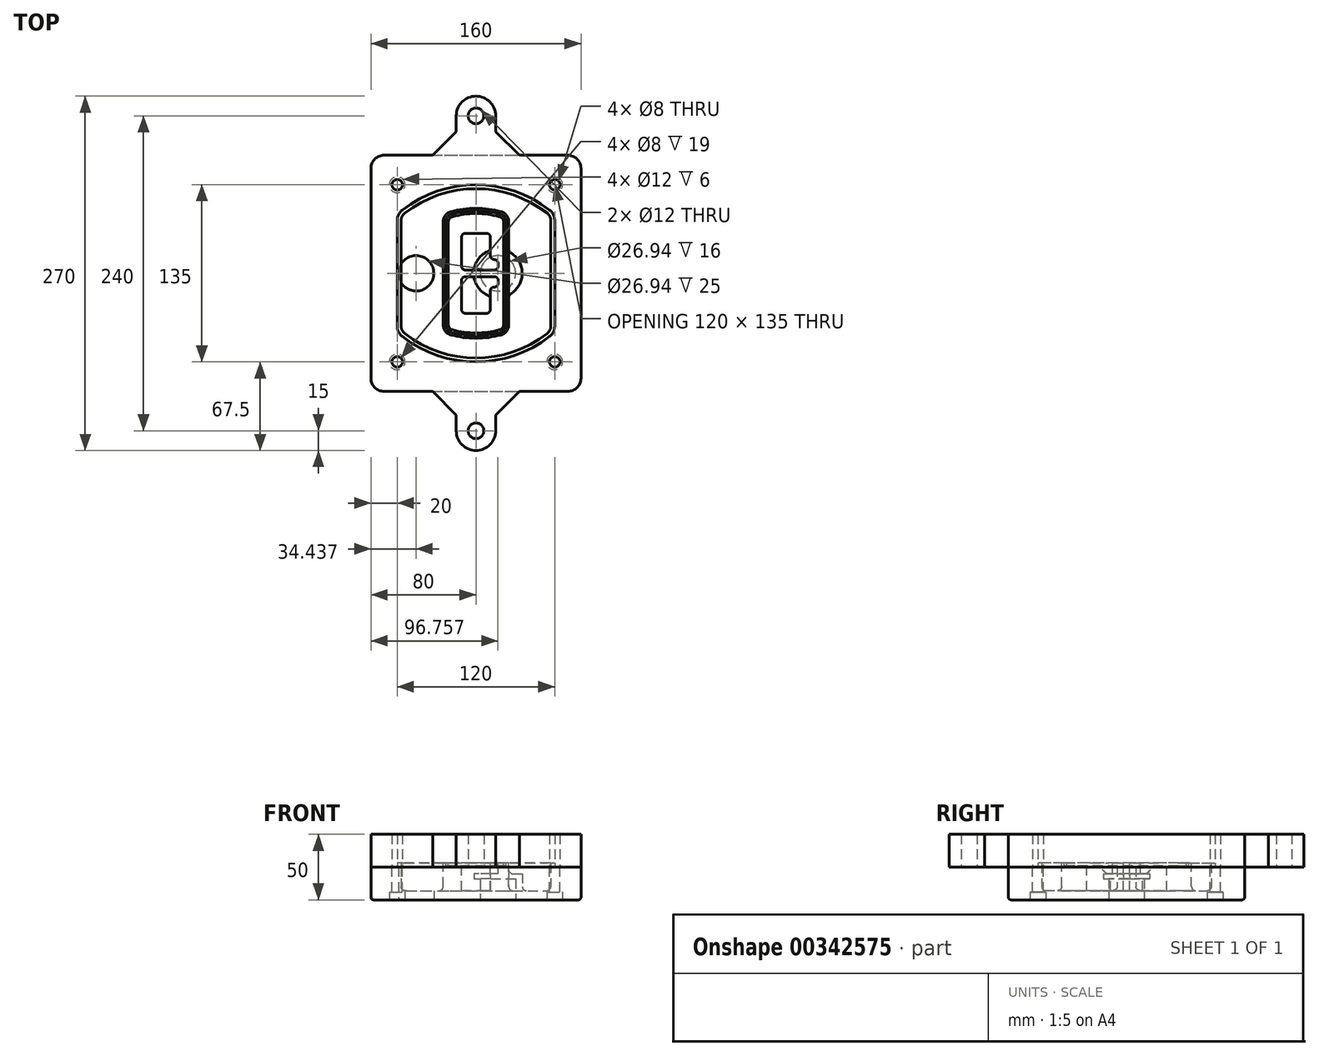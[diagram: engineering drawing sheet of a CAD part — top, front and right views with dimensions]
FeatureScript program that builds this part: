
annotation { "Feature Type Name" : "Feature", "Feature Type Description" : "" }
export const myFeature = defineFeature(function(context is Context, id is Id, definition is map)
    precondition{}
    {
        {
            var Q0;
            Q0=qCreatedBy(makeId("Top.planeOp"),FACE);
            var sketch = newSketch(context, id + "F0", { "sketchPlane" : qUnion([Q0])});
            skPoint(sketch, "E0.rect.middle", {"position": v(0, 0) * mm});
            skLineSegment(sketch, "E1.bottom", {"start": v(-70, -90) * mm, "end": v(70, -90) * mm});
            skLineSegment(sketch, "E1.top", {"start": v(-70, 90) * mm, "end": v(70, 90) * mm});
            skLineSegment(sketch, "E1.left", {"start": v(-80, -80) * mm, "end": v(-80, 80) * mm});
            skLineSegment(sketch, "E1.right", {"start": v(80, -80) * mm, "end": v(80, 80) * mm});
            skLineSegment(sketch, "E2", {"start": v(-80, 90) * mm, "end": v(80, -90) * mm, "construction": true});
            skLineSegment(sketch, "E3", {"start": v(80, 90) * mm, "end": v(-80, -90) * mm, "construction": true});
            skCircle(sketch, "E4", {"center": v(-60, 67.5) * mm, "radius": 4 * mm});
            skCircle(sketch, "E5", {"center": v(60, 67.5) * mm, "radius": 4 * mm});
            skCircle(sketch, "E6", {"center": v(60, -67.5) * mm, "radius": 4 * mm});
            skCircle(sketch, "E7", {"center": v(-60, -67.5) * mm, "radius": 4 * mm});
            skLineSegment(sketch, "E8", {"start": v(-60, 67.5) * mm, "end": v(60, 67.5) * mm, "construction": true});
            skLineSegment(sketch, "E9", {"start": v(60, 67.5) * mm, "end": v(60, -67.5) * mm, "construction": true});
            skLineSegment(sketch, "E10", {"start": v(60, -67.5) * mm, "end": v(-60, -67.5) * mm, "construction": true});
            skLineSegment(sketch, "E11", {"start": v(-60, -67.5) * mm, "end": v(-60, 67.5) * mm, "construction": true});
            skLineSegment(sketch, "E12", {"start": v(-60, 40.3) * mm, "end": v(-60, -40.3) * mm});
            skLineSegment(sketch, "E13", {"start": v(60, 40.3) * mm, "end": v(60, -40.3) * mm});
            skArc(sketch, "E14", {"start": v(56.15, 48.18) * mm, "mid": v(0, 67.5) * mm, "end": v(-56.15, 48.18) * mm});
            skArc(sketch, "E15", {"start": v(-56.15, -48.18) * mm, "mid": v(0, -67.5) * mm, "end": v(56.15, -48.18) * mm});
            skLineSegment(sketch, "E16", {"start": v(-60, 0) * mm, "end": v(60, 0) * mm, "construction": true});
            skPoint(sketch, "E17.visualSharp", {"position": v(-60, -45) * mm});
            skArc(sketch, "E17.filletArc", {"start": v(-60, -40.3) * mm, "mid": v(-58.99, -44.68) * mm, "end": v(-56.15, -48.18) * mm});
            skPoint(sketch, "E18.visualSharp", {"position": v(-60, 45) * mm});
            skArc(sketch, "E18.filletArc", {"start": v(-56.15, 48.18) * mm, "mid": v(-58.99, 44.68) * mm, "end": v(-60, 40.3) * mm});
            skPoint(sketch, "E19.visualSharp", {"position": v(60, 45) * mm});
            skArc(sketch, "E19.filletArc", {"start": v(60, 40.3) * mm, "mid": v(58.99, 44.68) * mm, "end": v(56.15, 48.18) * mm});
            skPoint(sketch, "E20.visualSharp", {"position": v(60, -45) * mm});
            skArc(sketch, "E20.filletArc", {"start": v(56.15, -48.18) * mm, "mid": v(58.99, -44.68) * mm, "end": v(60, -40.3) * mm});
            skPoint(sketch, "E21.visualSharp", {"position": v(-80, 90) * mm});
            skArc(sketch, "E21.filletArc", {"start": v(-70, 90) * mm, "mid": v(-77.07, 87.07) * mm, "end": v(-80, 80) * mm});
            skPoint(sketch, "E22.visualSharp", {"position": v(80, 90) * mm});
            skArc(sketch, "E22.filletArc", {"start": v(80, 80) * mm, "mid": v(77.07, 87.07) * mm, "end": v(70, 90) * mm});
            skPoint(sketch, "E23.visualSharp", {"position": v(80, -90) * mm});
            skArc(sketch, "E23.filletArc", {"start": v(70, -90) * mm, "mid": v(77.07, -87.07) * mm, "end": v(80, -80) * mm});
            skPoint(sketch, "E24.visualSharp", {"position": v(-80, -90) * mm});
            skArc(sketch, "E24.filletArc", {"start": v(-80, -80) * mm, "mid": v(-77.07, -87.07) * mm, "end": v(-70, -90) * mm});
            skArc(sketch, "E25.0", {"start": v(57, 40.3) * mm, "mid": v(56.3, 43.36) * mm, "end": v(54.3, 45.81) * mm});
            skLineSegment(sketch, "E25.1", {"start": v(57, 40.3) * mm, "end": v(57, -40.3) * mm});
            skArc(sketch, "E25.2", {"start": v(54.3, -45.81) * mm, "mid": v(56.3, -43.36) * mm, "end": v(57, -40.3) * mm});
            skArc(sketch, "E25.3", {"start": v(-54.3, -45.81) * mm, "mid": v(0, -64.5) * mm, "end": v(54.3, -45.81) * mm});
            skArc(sketch, "E25.4", {"start": v(-57, -40.3) * mm, "mid": v(-56.3, -43.36) * mm, "end": v(-54.3, -45.81) * mm});
            skArc(sketch, "E25.5", {"start": v(54.3, 45.81) * mm, "mid": v(0, 64.5) * mm, "end": v(-54.3, 45.81) * mm});
            skLineSegment(sketch, "E25.6", {"start": v(-57, 40.3) * mm, "end": v(-57, -40.3) * mm});
            skArc(sketch, "E25.7", {"start": v(-54.3, 45.81) * mm, "mid": v(-56.3, 43.36) * mm, "end": v(-57, 40.3) * mm});
            skArc(sketch, "E26.0", {"start": v(-58.62, 51.33) * mm, "mid": v(-62.58, 46.43) * mm, "end": v(-64, 40.3) * mm});
            skArc(sketch, "E26.1", {"start": v(58.62, 51.33) * mm, "mid": v(0, 71.5) * mm, "end": v(-58.62, 51.33) * mm});
            skArc(sketch, "E26.2", {"start": v(64, 40.3) * mm, "mid": v(62.58, 46.43) * mm, "end": v(58.62, 51.33) * mm});
            skLineSegment(sketch, "E26.3", {"start": v(64, 40.3) * mm, "end": v(64, -40.3) * mm});
            skArc(sketch, "E26.4", {"start": v(58.62, -51.33) * mm, "mid": v(62.58, -46.43) * mm, "end": v(64, -40.3) * mm});
            skLineSegment(sketch, "E26.5", {"start": v(-64, 40.3) * mm, "end": v(-64, -40.3) * mm});
            skArc(sketch, "E26.6", {"start": v(-58.62, -51.33) * mm, "mid": v(0, -71.5) * mm, "end": v(58.62, -51.33) * mm});
            skArc(sketch, "E26.7", {"start": v(-64, -40.3) * mm, "mid": v(-62.58, -46.43) * mm, "end": v(-58.62, -51.33) * mm});
            skSolve(sketch);
        }
        {
            var Q0;
            Q0=makeQuery(id+"F0.imprint","IMPRINT",FACE,{"disambiguationData":[TD([[makeQuery(id+"F0.imprint","IMPRINT",EDGE,{"derivedFrom":sQuery(id+"F0.wireOp",EDGE,"E1.bottom")}),1.0]])]});
            var Q1;
            Q1=makeQuery(id+"F0.imprint","IMPRINT",FACE,{"disambiguationData":[TD([[makeQuery(id+"F0.imprint","IMPRINT",EDGE,{"derivedFrom":sQuery(id+"F0.wireOp",EDGE,"E12")}),1.0]])]});
            var Q2;
            Q2=makeQuery(id+"F0.imprint","IMPRINT",FACE,{"disambiguationData":[TD([[makeQuery(id+"F0.imprint","IMPRINT",EDGE,{"derivedFrom":sQuery(id+"F0.wireOp",EDGE,"E25.0")}),1.0]])]});
            var Q3;
            Q3=makeQuery(id+"F0.imprint","IMPRINT",FACE,{"disambiguationData":[TD([[makeQuery(id+"F0.imprint","IMPRINT",EDGE,{"derivedFrom":sQuery(id+"F0.wireOp",EDGE,"E12")}),-1.0]])]});
            extrude(context, id + "F1", {"entities" : qUnion([Q0, Q1, Q2, Q3]), "oppositeDirection" : true, "depth" : 25 * mm});
        }
        {
            var Q0;
            Q0=makeQuery(id+"F0.imprint","IMPRINT",FACE,{"disambiguationData":[TD([[makeQuery(id+"F0.imprint","IMPRINT",EDGE,{"derivedFrom":sQuery(id+"F0.wireOp",EDGE,"E12")}),1.0]])]});
            extrude(context, id + "F2", {"entities" : qUnion([Q0]), "operationType" : NewBodyOperationType.ADD, "depth" : 3 * mm});
        }
        {
            var Q0;
            Q0=makeQuery(id+"F0.imprint","IMPRINT",FACE,{"disambiguationData":[TD([[makeQuery(id+"F0.imprint","IMPRINT",EDGE,{"derivedFrom":sQuery(id+"F0.wireOp",EDGE,"E25.0")}),1.0]])]});
            extrude(context, id + "F3", {"entities" : qUnion([Q0]), "operationType" : NewBodyOperationType.REMOVE, "oppositeDirection" : true, "depth" : 18 * mm});
        }
        {
            var Q0;
            Q0=makeQuery(id+"F2.opExtrude","CAP_FACE",FACE,{"disambiguationData":[OSD([sQuery(id+"F0.wireOp",EDGE,"E12"),sQuery(id+"F0.wireOp",EDGE,"E13"),sQuery(id+"F0.wireOp",EDGE,"E14"),sQuery(id+"F0.wireOp",EDGE,"E15"),sQuery(id+"F0.wireOp",EDGE,"E17.filletArc"),sQuery(id+"F0.wireOp",EDGE,"E18.filletArc"),sQuery(id+"F0.wireOp",EDGE,"E19.filletArc"),sQuery(id+"F0.wireOp",EDGE,"E20.filletArc"),sQuery(id+"F0.wireOp",EDGE,"E25.0"),sQuery(id+"F0.wireOp",EDGE,"E25.1"),sQuery(id+"F0.wireOp",EDGE,"E25.2"),sQuery(id+"F0.wireOp",EDGE,"E25.3"),sQuery(id+"F0.wireOp",EDGE,"E25.4"),sQuery(id+"F0.wireOp",EDGE,"E25.5"),sQuery(id+"F0.wireOp",EDGE,"E25.6"),sQuery(id+"F0.wireOp",EDGE,"E25.7")])],"isStart":false});
            var sketch = newSketch(context, id + "F4", { "sketchPlane" : qUnion([Q0])});
            skArc(sketch, "E27.0", {"start": v(-19.08, -46.97) * mm, "mid": v(0, -49.5) * mm, "end": v(19.08, -46.97) * mm});
            skArc(sketch, "E28.0", {"start": v(19.08, 46.97) * mm, "mid": v(0, 49.5) * mm, "end": v(-19.08, 46.97) * mm});
            skLineSegment(sketch, "E29", {"start": v(-25, 39.25) * mm, "end": v(-25, -39.25) * mm});
            skLineSegment(sketch, "E30", {"start": v(25, 39.25) * mm, "end": v(25, -39.25) * mm});
            skLineSegment(sketch, "E31", {"start": v(-25, 45.1) * mm, "end": v(25, 45.1) * mm, "construction": true});
            skLineSegment(sketch, "E32", {"start": v(-25, -45.1) * mm, "end": v(25, -45.1) * mm, "construction": true});
            skPoint(sketch, "E33.visualSharp", {"position": v(-25, 45.1) * mm});
            skArc(sketch, "E33.filletArc", {"start": v(-19.08, 46.97) * mm, "mid": v(-23.35, 44.11) * mm, "end": v(-25, 39.25) * mm});
            skPoint(sketch, "E34.visualSharp", {"position": v(25, 45.1) * mm});
            skArc(sketch, "E34.filletArc", {"start": v(25, 39.25) * mm, "mid": v(23.35, 44.11) * mm, "end": v(19.08, 46.97) * mm});
            skPoint(sketch, "E35.visualSharp", {"position": v(25, -45.1) * mm});
            skArc(sketch, "E35.filletArc", {"start": v(19.08, -46.97) * mm, "mid": v(23.35, -44.11) * mm, "end": v(25, -39.25) * mm});
            skPoint(sketch, "E36.visualSharp", {"position": v(-25, -45.1) * mm});
            skArc(sketch, "E36.filletArc", {"start": v(-25, -39.25) * mm, "mid": v(-23.35, -44.11) * mm, "end": v(-19.08, -46.97) * mm});
            skArc(sketch, "E37.0", {"start": v(54.3, 45.81) * mm, "mid": v(0, 64.5) * mm, "end": v(-54.3, 45.81) * mm});
            skArc(sketch, "E37.1", {"start": v(-54.3, 45.81) * mm, "mid": v(-56.3, 43.36) * mm, "end": v(-57, 40.3) * mm});
            skLineSegment(sketch, "E37.2", {"start": v(-57, 40.3) * mm, "end": v(-57, -40.3) * mm});
            skArc(sketch, "E37.3", {"start": v(-57, -40.3) * mm, "mid": v(-56.3, -43.36) * mm, "end": v(-54.3, -45.81) * mm});
            skArc(sketch, "E37.4", {"start": v(-54.3, -45.81) * mm, "mid": v(0, -64.5) * mm, "end": v(54.3, -45.81) * mm});
            skArc(sketch, "E37.5", {"start": v(54.3, -45.81) * mm, "mid": v(56.3, -43.36) * mm, "end": v(57, -40.3) * mm});
            skLineSegment(sketch, "E37.6", {"start": v(57, 40.3) * mm, "end": v(57, -40.3) * mm});
            skArc(sketch, "E37.7", {"start": v(57, 40.3) * mm, "mid": v(56.3, 43.36) * mm, "end": v(54.3, 45.81) * mm});
            skLineSegment(sketch, "E38.0", {"start": v(23, 39.25) * mm, "end": v(23, -39.25) * mm});
            skArc(sketch, "E38.1", {"start": v(18.56, -45.04) * mm, "mid": v(21.76, -42.9) * mm, "end": v(23, -39.25) * mm});
            skArc(sketch, "E38.2", {"start": v(-18.56, -45.04) * mm, "mid": v(0, -47.5) * mm, "end": v(18.56, -45.04) * mm});
            skArc(sketch, "E38.3", {"start": v(-23, -39.25) * mm, "mid": v(-21.76, -42.9) * mm, "end": v(-18.56, -45.04) * mm});
            skLineSegment(sketch, "E38.4", {"start": v(-23, 39.25) * mm, "end": v(-23, -39.25) * mm});
            skArc(sketch, "E38.5", {"start": v(23, 39.25) * mm, "mid": v(21.76, 42.9) * mm, "end": v(18.56, 45.04) * mm});
            skArc(sketch, "E38.6", {"start": v(-18.56, 45.04) * mm, "mid": v(-21.76, 42.9) * mm, "end": v(-23, 39.25) * mm});
            skArc(sketch, "E38.7", {"start": v(18.56, 45.04) * mm, "mid": v(0, 47.5) * mm, "end": v(-18.56, 45.04) * mm});
            skArc(sketch, "E39.0", {"start": v(21, 39.25) * mm, "mid": v(20.18, 41.68) * mm, "end": v(18.04, 43.1) * mm});
            skLineSegment(sketch, "E39.1", {"start": v(21, 39.25) * mm, "end": v(21, -39.25) * mm});
            skArc(sketch, "E39.2", {"start": v(18.04, -43.1) * mm, "mid": v(20.18, -41.68) * mm, "end": v(21, -39.25) * mm});
            skArc(sketch, "E39.3", {"start": v(-18.04, -43.1) * mm, "mid": v(0, -45.5) * mm, "end": v(18.04, -43.1) * mm});
            skArc(sketch, "E39.4", {"start": v(-21, -39.25) * mm, "mid": v(-20.18, -41.68) * mm, "end": v(-18.04, -43.1) * mm});
            skArc(sketch, "E39.5", {"start": v(18.04, 43.1) * mm, "mid": v(0, 45.5) * mm, "end": v(-18.04, 43.1) * mm});
            skLineSegment(sketch, "E39.6", {"start": v(-21, 39.25) * mm, "end": v(-21, -39.25) * mm});
            skArc(sketch, "E39.7", {"start": v(-18.04, 43.1) * mm, "mid": v(-20.18, 41.68) * mm, "end": v(-21, 39.25) * mm});
            skLineSegment(sketch, "E40", {"start": v(-25, 0) * mm, "end": v(25, 0) * mm, "construction": true});
            skLineSegment(sketch, "E41", {"start": v(-11, 5.5) * mm, "end": v(-11, 27.5) * mm});
            skLineSegment(sketch, "E42", {"start": v(-8, 30.5) * mm, "end": v(8, 30.5) * mm});
            skLineSegment(sketch, "E43", {"start": v(11, 27.5) * mm, "end": v(11, 13.5) * mm});
            skLineSegment(sketch, "E44", {"start": v(14, 10.5) * mm, "end": v(14, 10.5) * mm});
            skLineSegment(sketch, "E45", {"start": v(17, 7.5) * mm, "end": v(17, 5.5) * mm});
            skLineSegment(sketch, "E46", {"start": v(14, 2.5) * mm, "end": v(-8, 2.5) * mm});
            skPoint(sketch, "E47.visualSharp", {"position": v(-11, 30.5) * mm});
            skArc(sketch, "E47.filletArc", {"start": v(-8, 30.5) * mm, "mid": v(-10.12, 29.62) * mm, "end": v(-11, 27.5) * mm});
            skPoint(sketch, "E48.visualSharp", {"position": v(11, 30.5) * mm});
            skArc(sketch, "E48.filletArc", {"start": v(11, 27.5) * mm, "mid": v(10.12, 29.62) * mm, "end": v(8, 30.5) * mm});
            skPoint(sketch, "E49.visualSharp", {"position": v(11, 10.5) * mm});
            skArc(sketch, "E49.filletArc", {"start": v(11, 13.5) * mm, "mid": v(11.88, 11.38) * mm, "end": v(14, 10.5) * mm});
            skPoint(sketch, "E50.visualSharp", {"position": v(17, 10.5) * mm});
            skArc(sketch, "E50.filletArc", {"start": v(17, 7.5) * mm, "mid": v(16.12, 9.62) * mm, "end": v(14, 10.5) * mm});
            skPoint(sketch, "E51.visualSharp", {"position": v(17, 2.5) * mm});
            skArc(sketch, "E51.filletArc", {"start": v(14, 2.5) * mm, "mid": v(16.12, 3.38) * mm, "end": v(17, 5.5) * mm});
            skPoint(sketch, "E52.visualSharp", {"position": v(-11, 2.5) * mm});
            skArc(sketch, "E52.filletArc", {"start": v(-11, 5.5) * mm, "mid": v(-10.12, 3.38) * mm, "end": v(-8, 2.5) * mm});
            skLineSegment(sketch, "E53.0.MirrorCS", {"start": v(14, -2.5) * mm, "end": v(-8, -2.5) * mm});
            skArc(sketch, "E54.0.MirrorCS", {"start": v(-11, -5.5) * mm, "mid": v(-10.12, -3.38) * mm, "end": v(-8, -2.5) * mm});
            skLineSegment(sketch, "E55.0.MirrorCS", {"start": v(-11, -5.5) * mm, "end": v(-11, -27.5) * mm});
            skArc(sketch, "E56.0.MirrorCS", {"start": v(-8, -30.5) * mm, "mid": v(-10.12, -29.62) * mm, "end": v(-11, -27.5) * mm});
            skLineSegment(sketch, "E57.0.MirrorCS", {"start": v(-8, -30.5) * mm, "end": v(8, -30.5) * mm});
            skArc(sketch, "E58.0.MirrorCS", {"start": v(11, -27.5) * mm, "mid": v(10.12, -29.62) * mm, "end": v(8, -30.5) * mm});
            skLineSegment(sketch, "E59.0.MirrorCS", {"start": v(11, -27.5) * mm, "end": v(11, -13.5) * mm});
            skArc(sketch, "E60.0.MirrorCS", {"start": v(11, -13.5) * mm, "mid": v(11.88, -11.38) * mm, "end": v(14, -10.5) * mm});
            skArc(sketch, "E61.0.MirrorCS", {"start": v(17, -7.5) * mm, "mid": v(16.12, -9.62) * mm, "end": v(14, -10.5) * mm});
            skLineSegment(sketch, "E62.0.MirrorCS", {"start": v(17, -7.5) * mm, "end": v(17, -5.5) * mm});
            skArc(sketch, "E63.0.MirrorCS", {"start": v(14, -2.5) * mm, "mid": v(16.12, -3.38) * mm, "end": v(17, -5.5) * mm});
            skSolve(sketch);
        }
        {
            var Q0;
            Q0=makeQuery(id+"F4.imprint","IMPRINT",FACE,{"disambiguationData":[TD([[makeQuery(id+"F4.imprint","IMPRINT",EDGE,{"derivedFrom":sQuery(id+"F4.wireOp",EDGE,"E27.0")}),1.0]])]});
            var Q1;
            Q1=makeQuery(id+"F4.imprint","IMPRINT",FACE,{"disambiguationData":[TD([[makeQuery(id+"F4.imprint","IMPRINT",EDGE,{"derivedFrom":sQuery(id+"F4.wireOp",EDGE,"E38.0")}),-1.0]])]});
            var Q2;
            Q2=makeQuery(id+"F4.imprint","IMPRINT",FACE,{"disambiguationData":[TD([[makeQuery(id+"F4.imprint","IMPRINT",EDGE,{"derivedFrom":sQuery(id+"F4.wireOp",EDGE,"E39.0")}),1.0]])]});
            extrude(context, id + "F5", {"entities" : qUnion([Q0, Q1, Q2]), "operationType" : NewBodyOperationType.ADD, "endBound" : BoundingType.UP_TO_NEXT, "oppositeDirection" : true, "depth" : 25 * mm});
        }
        {
            var Q0;
            Q0=makeQuery(id+"F4.imprint","IMPRINT",FACE,{"disambiguationData":[TD([[makeQuery(id+"F4.imprint","IMPRINT",EDGE,{"derivedFrom":sQuery(id+"F4.wireOp",EDGE,"E38.0")}),-1.0]])]});
            extrude(context, id + "F6", {"entities" : qUnion([Q0]), "operationType" : NewBodyOperationType.REMOVE, "oppositeDirection" : true, "depth" : 2 * mm});
        }
        {
            var Q0;
            Q0=makeQuery(id+"F1.opExtrude","CAP_FACE",FACE,{"disambiguationData":[OSD([sQuery(id+"F0.wireOp",EDGE,"E1.bottom"),sQuery(id+"F0.wireOp",EDGE,"E1.top"),sQuery(id+"F0.wireOp",EDGE,"E1.left"),sQuery(id+"F0.wireOp",EDGE,"E1.right"),sQuery(id+"F0.wireOp",EDGE,"E4"),sQuery(id+"F0.wireOp",EDGE,"E5"),sQuery(id+"F0.wireOp",EDGE,"E6"),sQuery(id+"F0.wireOp",EDGE,"E7"),sQuery(id+"F0.wireOp",EDGE,"E21.filletArc"),sQuery(id+"F0.wireOp",EDGE,"E22.filletArc"),sQuery(id+"F0.wireOp",EDGE,"E23.filletArc"),sQuery(id+"F0.wireOp",EDGE,"E24.filletArc")])],"isStart":false});
            var sketch = newSketch(context, id + "F7", { "sketchPlane" : qUnion([Q0])});
            skCircle(sketch, "E64", {"center": v(16.76, 0) * mm, "radius": 13.47 * mm});
            skCircle(sketch, "E65", {"center": v(-45.56, 0) * mm, "radius": 13.47 * mm});
            skLineSegment(sketch, "E66", {"start": v(80, 0) * mm, "end": v(-80, 0) * mm});
            skCircle(sketch, "E67", {"center": v(16.76, 0) * mm, "radius": 18.47 * mm});
            skCircle(sketch, "E68", {"center": v(60, -67.5) * mm, "radius": 6 * mm});
            skCircle(sketch, "E69", {"center": v(-60, -67.5) * mm, "radius": 6 * mm});
            skCircle(sketch, "E70", {"center": v(-60, 67.5) * mm, "radius": 6 * mm});
            skCircle(sketch, "E71", {"center": v(60, 67.5) * mm, "radius": 6 * mm});
            skSolve(sketch);
        }
        {
            var Q0;
            {var subQ1=sQuery(id+"F7.wireOp",EDGE,"E66");var subQ4=sQuery(id+"F7.wireOp",EDGE,"E64");var subQ6=makeQuery(id+"F7.imprint","INTERSECT",VERTEX,{"disambiguationData":[OD(0.0)],"derivedFrom":[subQ4,subQ1]});Q0=makeQuery(id+"F7.imprint","IMPRINT",FACE,{"disambiguationData":[TD([[makeQuery(id+"F7.imprint","IMPRINT",EDGE,{"disambiguationData":[TD([[subQ6,-1.0]])],"derivedFrom":subQ4}),-1.0]])]});}
            var Q1;
            {var subQ0=sQuery(id+"F7.wireOp",EDGE,"E66");var subQ1=sQuery(id+"F7.wireOp",EDGE,"E64");var subQ3=makeQuery(id+"F7.imprint","INTERSECT",VERTEX,{"disambiguationData":[OD(0.0)],"derivedFrom":[subQ1,subQ0]});Q1=makeQuery(id+"F7.imprint","IMPRINT",FACE,{"disambiguationData":[TD([[makeQuery(id+"F7.imprint","IMPRINT",EDGE,{"disambiguationData":[TD([[subQ3,-1.0]])],"derivedFrom":subQ1}),1.0]])]});}
            var Q2;
            {var subQ0=sQuery(id+"F7.wireOp",EDGE,"E66");var subQ1=sQuery(id+"F7.wireOp",EDGE,"E64");var subQ3=makeQuery(id+"F7.imprint","INTERSECT",VERTEX,{"disambiguationData":[OD(0.0)],"derivedFrom":[subQ1,subQ0]});Q2=makeQuery(id+"F7.imprint","IMPRINT",FACE,{"disambiguationData":[TD([[makeQuery(id+"F7.imprint","IMPRINT",EDGE,{"disambiguationData":[TD([[subQ3,1.0]])],"derivedFrom":subQ1}),1.0]])]});}
            var Q3;
            {var subQ1=sQuery(id+"F7.wireOp",EDGE,"E66");var subQ4=sQuery(id+"F7.wireOp",EDGE,"E64");var subQ6=makeQuery(id+"F7.imprint","INTERSECT",VERTEX,{"disambiguationData":[OD(0.0)],"derivedFrom":[subQ4,subQ1]});Q3=makeQuery(id+"F7.imprint","IMPRINT",FACE,{"disambiguationData":[TD([[makeQuery(id+"F7.imprint","IMPRINT",EDGE,{"disambiguationData":[TD([[subQ6,1.0]])],"derivedFrom":subQ4}),-1.0]])]});}
            extrude(context, id + "F8", {"entities" : qUnion([Q0, Q1, Q2, Q3]), "operationType" : NewBodyOperationType.ADD, "oppositeDirection" : true, "depth" : 20 * mm});
        }
        {
            var Q0;
            {var subQ0=sQuery(id+"F7.wireOp",EDGE,"E66");var subQ1=sQuery(id+"F7.wireOp",EDGE,"E64");var subQ3=makeQuery(id+"F7.imprint","INTERSECT",VERTEX,{"disambiguationData":[OD(0.0)],"derivedFrom":[subQ1,subQ0]});Q0=makeQuery(id+"F7.imprint","IMPRINT",FACE,{"disambiguationData":[TD([[makeQuery(id+"F7.imprint","IMPRINT",EDGE,{"disambiguationData":[TD([[subQ3,-1.0]])],"derivedFrom":subQ1}),1.0]])]});}
            var Q1;
            {var subQ0=sQuery(id+"F7.wireOp",EDGE,"E66");var subQ1=sQuery(id+"F7.wireOp",EDGE,"E64");var subQ3=makeQuery(id+"F7.imprint","INTERSECT",VERTEX,{"disambiguationData":[OD(0.0)],"derivedFrom":[subQ1,subQ0]});Q1=makeQuery(id+"F7.imprint","IMPRINT",FACE,{"disambiguationData":[TD([[makeQuery(id+"F7.imprint","IMPRINT",EDGE,{"disambiguationData":[TD([[subQ3,1.0]])],"derivedFrom":subQ1}),1.0]])]});}
            extrude(context, id + "F9", {"entities" : qUnion([Q0, Q1]), "operationType" : NewBodyOperationType.REMOVE, "oppositeDirection" : true, "depth" : 16 * mm});
        }
        {
            var Q0;
            {var subQ0=sQuery(id+"F7.wireOp",EDGE,"E66");var subQ1=sQuery(id+"F7.wireOp",EDGE,"E65");var subQ3=makeQuery(id+"F7.imprint","INTERSECT",VERTEX,{"disambiguationData":[OD(0.0)],"derivedFrom":[subQ1,subQ0]});Q0=makeQuery(id+"F7.imprint","IMPRINT",FACE,{"disambiguationData":[TD([[makeQuery(id+"F7.imprint","IMPRINT",EDGE,{"disambiguationData":[TD([[subQ3,-1.0]])],"derivedFrom":subQ1}),1.0]])]});}
            var Q1;
            {var subQ0=sQuery(id+"F7.wireOp",EDGE,"E66");var subQ1=sQuery(id+"F7.wireOp",EDGE,"E65");var subQ3=makeQuery(id+"F7.imprint","INTERSECT",VERTEX,{"disambiguationData":[OD(0.0)],"derivedFrom":[subQ1,subQ0]});Q1=makeQuery(id+"F7.imprint","IMPRINT",FACE,{"disambiguationData":[TD([[makeQuery(id+"F7.imprint","IMPRINT",EDGE,{"disambiguationData":[TD([[subQ3,1.0]])],"derivedFrom":subQ1}),1.0]])]});}
            extrude(context, id + "F10", {"entities" : qUnion([Q0, Q1]), "operationType" : NewBodyOperationType.REMOVE, "oppositeDirection" : true, "depth" : 25 * mm});
        }
        {
            var Q0;
            Q0=makeQuery(id+"F7.imprint","IMPRINT",FACE,{"disambiguationData":[TD([[makeQuery(id+"F7.imprint","IMPRINT",EDGE,{"derivedFrom":sQuery(id+"F7.wireOp",EDGE,"E68")}),1.0]])]});
            var Q1;
            Q1=makeQuery(id+"F7.imprint","IMPRINT",FACE,{"disambiguationData":[TD([[makeQuery(id+"F7.imprint","IMPRINT",EDGE,{"derivedFrom":makeQuery(id+"F1.opExtrude","CAP_EDGE",EDGE,{"disambiguationData":[OSD([sQuery(id+"F0.wireOp",EDGE,"E5")])],"isStart":false})}),-1.0]])]});
            var Q2;
            Q2=makeQuery(id+"F7.imprint","IMPRINT",FACE,{"disambiguationData":[TD([[makeQuery(id+"F7.imprint","IMPRINT",EDGE,{"derivedFrom":sQuery(id+"F7.wireOp",EDGE,"E69")}),1.0]])]});
            var Q3;
            Q3=makeQuery(id+"F7.imprint","IMPRINT",FACE,{"disambiguationData":[TD([[makeQuery(id+"F7.imprint","IMPRINT",EDGE,{"derivedFrom":makeQuery(id+"F1.opExtrude","CAP_EDGE",EDGE,{"disambiguationData":[OSD([sQuery(id+"F0.wireOp",EDGE,"E4")])],"isStart":false})}),-1.0]])]});
            var Q4;
            Q4=makeQuery(id+"F7.imprint","IMPRINT",FACE,{"disambiguationData":[TD([[makeQuery(id+"F7.imprint","IMPRINT",EDGE,{"derivedFrom":sQuery(id+"F7.wireOp",EDGE,"E70")}),1.0]])]});
            var Q5;
            Q5=makeQuery(id+"F7.imprint","IMPRINT",FACE,{"disambiguationData":[TD([[makeQuery(id+"F7.imprint","IMPRINT",EDGE,{"derivedFrom":makeQuery(id+"F1.opExtrude","CAP_EDGE",EDGE,{"disambiguationData":[OSD([sQuery(id+"F0.wireOp",EDGE,"E7")])],"isStart":false})}),-1.0]])]});
            var Q6;
            Q6=makeQuery(id+"F7.imprint","IMPRINT",FACE,{"disambiguationData":[TD([[makeQuery(id+"F7.imprint","IMPRINT",EDGE,{"derivedFrom":sQuery(id+"F7.wireOp",EDGE,"E71")}),1.0]])]});
            var Q7;
            Q7=makeQuery(id+"F7.imprint","IMPRINT",FACE,{"disambiguationData":[TD([[makeQuery(id+"F7.imprint","IMPRINT",EDGE,{"derivedFrom":makeQuery(id+"F1.opExtrude","CAP_EDGE",EDGE,{"disambiguationData":[OSD([sQuery(id+"F0.wireOp",EDGE,"E6")])],"isStart":false})}),-1.0]])]});
            extrude(context, id + "F11", {"entities" : qUnion([Q0, Q1, Q2, Q3, Q4, Q5, Q6, Q7]), "operationType" : NewBodyOperationType.REMOVE, "oppositeDirection" : true, "depth" : 6 * mm});
        }
        {
            var Q0;
            Q0=makeQuery(id+"F9.boolean.opBoolean","COPY",FACE,{"derivedFrom":makeQuery(id+"F9.opExtrude","CAP_FACE",FACE,{"disambiguationData":[OSD([sQuery(id+"F7.wireOp",EDGE,"E64")])],"isStart":false})});
            var sketch = newSketch(context, id + "F12", { "sketchPlane" : qUnion([Q0])});
            skArc(sketch, "E72.0", {"start": v(11, 17.55) * mm, "mid": v(2.57, 11.82) * mm, "end": v(-1.54, 2.5) * mm});
            skArc(sketch, "E72.1", {"start": v(-1.54, -2.5) * mm, "mid": v(2.57, -11.82) * mm, "end": v(11, -17.55) * mm});
            skLineSegment(sketch, "E73", {"start": v(-1.54, -2.5) * mm, "end": v(14, -2.5) * mm});
            skLineSegment(sketch, "E74.0", {"start": v(14, 2.5) * mm, "end": v(-1.54, 2.5) * mm});
            skArc(sketch, "E74.1", {"start": v(14, 2.5) * mm, "mid": v(16.12, 3.38) * mm, "end": v(17, 5.5) * mm});
            skLineSegment(sketch, "E74.2", {"start": v(17, 7.5) * mm, "end": v(17, 5.5) * mm});
            skArc(sketch, "E74.3", {"start": v(17, 7.5) * mm, "mid": v(16.12, 9.62) * mm, "end": v(14, 10.5) * mm});
            skArc(sketch, "E74.4", {"start": v(11, 13.5) * mm, "mid": v(11.88, 11.38) * mm, "end": v(14, 10.5) * mm});
            skLineSegment(sketch, "E74.5", {"start": v(11, 17.55) * mm, "end": v(11, 13.5) * mm});
            skLineSegment(sketch, "E74.7", {"start": v(14, -2.5) * mm, "end": v(-1.54, -2.5) * mm});
            skArc(sketch, "E74.8", {"start": v(14, -2.5) * mm, "mid": v(16.12, -3.38) * mm, "end": v(17, -5.5) * mm});
            skLineSegment(sketch, "E74.9", {"start": v(17, -7.5) * mm, "end": v(17, -5.5) * mm});
            skArc(sketch, "E74.10", {"start": v(17, -7.5) * mm, "mid": v(16.12, -9.62) * mm, "end": v(14, -10.5) * mm});
            skArc(sketch, "E74.11", {"start": v(11, -13.5) * mm, "mid": v(11.88, -11.38) * mm, "end": v(14, -10.5) * mm});
            skLineSegment(sketch, "E74.12", {"start": v(11, -17.55) * mm, "end": v(11, -13.5) * mm});
            skPoint(sketch, "E75.orphan", {"position": v(11, -27.5) * mm});
            skPoint(sketch, "E76.orphan", {"position": v(-8, -2.5) * mm});
            skPoint(sketch, "E77.orphan", {"position": v(-8, 2.5) * mm});
            skPoint(sketch, "E78.orphan", {"position": v(11, 27.5) * mm});
            skSolve(sketch);
        }
        {
            var Q0;
            {var subQ7=sQuery(id+"F12.wireOp",EDGE,"E72.0");var subQ14=sQuery(id+"F12.wireOp",EDGE,"E72.1");var subQ16=sQuery(id+"F12.wireOp",EDGE,"E74.1");var subQ18=sQuery(id+"F12.wireOp",EDGE,"E74.8");Q0=qUnion([makeQuery(id+"F12.imprint","IMPRINT",FACE,{"disambiguationData":[TD([[makeQuery(id+"F12.imprint","IMPRINT",EDGE,{"derivedFrom":subQ7}),1.0]])]}),makeQuery(id+"F12.imprint","IMPRINT",FACE,{"disambiguationData":[TD([[makeQuery(id+"F12.imprint","IMPRINT",EDGE,{"derivedFrom":subQ14}),1.0]])]}),makeQuery(id+"F12.imprint","IMPRINT",FACE,{"disambiguationData":[TD([[makeQuery(id+"F12.imprint","IMPRINT",EDGE,{"derivedFrom":subQ16}),1.0]])]}),makeQuery(id+"F12.imprint","IMPRINT",FACE,{"disambiguationData":[TD([[makeQuery(id+"F12.imprint","IMPRINT",EDGE,{"derivedFrom":subQ18}),-1.0]])]})]);}
            var Q1;
            Q1=makeQuery(id+"F5.boolean.opBoolean","SPLIT",FACE,{"disambiguationData":[TD([makeQuery(id+"F5.opExtrude","SWEPT_FACE",FACE,{"disambiguationData":[OSD([sQuery(id+"F4.wireOp",EDGE,"E41")])]})])],"derivedFrom":makeQuery(id+"F3.boolean.opBoolean","COPY",FACE,{"derivedFrom":makeQuery(id+"F3.opExtrude","CAP_FACE",FACE,{"disambiguationData":[OSD([sQuery(id+"F0.wireOp",EDGE,"E25.0"),sQuery(id+"F0.wireOp",EDGE,"E25.1"),sQuery(id+"F0.wireOp",EDGE,"E25.2"),sQuery(id+"F0.wireOp",EDGE,"E25.3"),sQuery(id+"F0.wireOp",EDGE,"E25.4"),sQuery(id+"F0.wireOp",EDGE,"E25.5"),sQuery(id+"F0.wireOp",EDGE,"E25.6"),sQuery(id+"F0.wireOp",EDGE,"E25.7")])],"isStart":false})})});
            extrude(context, id + "F13", {"entities" : qUnion([Q0]), "operationType" : NewBodyOperationType.REMOVE, "endBound" : BoundingType.UP_TO_SURFACE, "endBoundEntityFace" : qUnion([Q1]), "depth" : 25 * mm});
        }
        {
            var Q0;
            Q0=makeQuery(id+"F3.boolean.opBoolean","COPY",EDGE,{"derivedFrom":makeQuery(id+"F3.opExtrude","CAP_EDGE",EDGE,{"disambiguationData":[OSD([sQuery(id+"F0.wireOp",EDGE,"E25.6")])],"isStart":false})});
            var Q1;
            Q1=makeQuery(id+"F8.boolean.opBoolean","INTERSECT",EDGE,{"derivedFrom":[makeQuery(id+"F5.opExtrude","SWEPT_FACE",FACE,{"disambiguationData":[OSD([sQuery(id+"F4.wireOp",EDGE,"E30")])]}),makeQuery(id+"F8.opExtrude","CAP_FACE",FACE,{"disambiguationData":[OSD([sQuery(id+"F7.wireOp",EDGE,"E67")])],"isStart":false})]});
            var Q2;
            Q2=makeQuery(id+"F8.boolean.opBoolean","INTERSECT",EDGE,{"disambiguationData":[OD(1.0)],"derivedFrom":[makeQuery(id+"F5.opExtrude","SWEPT_FACE",FACE,{"disambiguationData":[OSD([sQuery(id+"F4.wireOp",EDGE,"E30")])]}),makeQuery(id+"F8.opExtrude","SWEPT_FACE",FACE,{"disambiguationData":[OSD([sQuery(id+"F7.wireOp",EDGE,"E67")])]})]});
            var Q3;
            {var subQ0=sQuery(id+"F4.wireOp",EDGE,"E30");Q3=makeQuery(id+"F8.boolean.opBoolean","SPLIT",EDGE,{"disambiguationData":[TD([makeQuery(id+"F5.opExtrude","SWEPT_FACE",FACE,{"disambiguationData":[OSD([sQuery(id+"F4.wireOp",EDGE,"E35.filletArc")])]})])],"derivedFrom":makeQuery(id+"F5.opExtrude","CAP_EDGE",EDGE,{"disambiguationData":[OSD([subQ0])],"isStart":false})});}
            var Q4;
            {var subQ0=sQuery(id+"F0.wireOp",EDGE,"E25.7");var subQ1=sQuery(id+"F0.wireOp",EDGE,"E25.1");var subQ2=sQuery(id+"F0.wireOp",EDGE,"E25.6");var subQ3=sQuery(id+"F0.wireOp",EDGE,"E25.5");var subQ4=sQuery(id+"F0.wireOp",EDGE,"E25.4");var subQ5=sQuery(id+"F0.wireOp",EDGE,"E25.0");var subQ6=sQuery(id+"F0.wireOp",EDGE,"E25.2");var subQ7=sQuery(id+"F0.wireOp",EDGE,"E25.3");Q4=makeQuery(id+"F8.boolean.opBoolean","INTERSECT",EDGE,{"derivedFrom":[makeQuery(id+"F5.boolean.opBoolean","SPLIT",FACE,{"disambiguationData":[TD([makeQuery(id+"F2.opExtrude","SWEPT_FACE",FACE,{"disambiguationData":[OSD([subQ5])]})])],"derivedFrom":makeQuery(id+"F3.boolean.opBoolean","COPY",FACE,{"derivedFrom":makeQuery(id+"F3.opExtrude","CAP_FACE",FACE,{"disambiguationData":[OSD([subQ5,subQ1,subQ6,subQ7,subQ4,subQ3,subQ2,subQ0])],"isStart":false})})}),makeQuery(id+"F8.opExtrude","SWEPT_FACE",FACE,{"disambiguationData":[OSD([sQuery(id+"F7.wireOp",EDGE,"E67")])]})]});}
            var Q5;
            Q5=makeQuery(id+"F8.boolean.opBoolean","INTERSECT",EDGE,{"disambiguationData":[OD(0.0)],"derivedFrom":[makeQuery(id+"F5.opExtrude","SWEPT_FACE",FACE,{"disambiguationData":[OSD([sQuery(id+"F4.wireOp",EDGE,"E30")])]}),makeQuery(id+"F8.opExtrude","SWEPT_FACE",FACE,{"disambiguationData":[OSD([sQuery(id+"F7.wireOp",EDGE,"E67")])]})]});
            fillet(context, id + "F14", {"entities" : qUnion([Q0, Q1, Q2, Q3, Q4, Q5]), "radius" : 3 * mm, "tangentPropagation" : true, "allowEdgeOverflow" : false});
        }
        {
            var Q0;
            Q0=makeQuery(id+"F1.opExtrude","CAP_EDGE",EDGE,{"disambiguationData":[OSD([sQuery(id+"F0.wireOp",EDGE,"E1.bottom")])],"isStart":false});
            fillet(context, id + "F15", {"entities" : qUnion([Q0]), "radius" : 2 * mm, "tangentPropagation" : true, "allowEdgeOverflow" : false});
        }
        {
            var Q0;
            {var subQ0=sQuery(id+"F0.wireOp",EDGE,"E21.filletArc");var subQ1=sQuery(id+"F0.wireOp",EDGE,"E7");var subQ2=sQuery(id+"F0.wireOp",EDGE,"E6");var subQ3=sQuery(id+"F0.wireOp",EDGE,"E5");var subQ4=sQuery(id+"F0.wireOp",EDGE,"E4");var subQ5=sQuery(id+"F0.wireOp",EDGE,"E22.filletArc");var subQ6=sQuery(id+"F0.wireOp",EDGE,"E1.bottom");var subQ7=sQuery(id+"F0.wireOp",EDGE,"E1.right");var subQ8=sQuery(id+"F0.wireOp",EDGE,"E1.top");var subQ9=sQuery(id+"F0.wireOp",EDGE,"E1.left");var subQ10=sQuery(id+"F0.wireOp",EDGE,"E23.filletArc");var subQ11=sQuery(id+"F0.wireOp",EDGE,"E24.filletArc");Q0=makeQuery(id+"F2.boolean.opBoolean","SPLIT",FACE,{"disambiguationData":[TD([makeQuery(id+"F1.opExtrude","SWEPT_FACE",FACE,{"disambiguationData":[OSD([subQ6])]})])],"derivedFrom":makeQuery(id+"F1.opExtrude","CAP_FACE",FACE,{"disambiguationData":[OSD([subQ6,subQ8,subQ9,subQ7,subQ4,subQ3,subQ2,subQ1,subQ0,subQ5,subQ10,subQ11])],"isStart":true})});}
            var sketch = newSketch(context, id + "F16", { "sketchPlane" : qUnion([Q0])});
            skLineSegment(sketch, "E79.0", {"start": v(57, 40.3) * mm, "end": v(57, -40.3) * mm});
            skLineSegment(sketch, "E80.0", {"start": v(-60, 40.3) * mm, "end": v(-60, -40.3) * mm});
            skArc(sketch, "E80.1", {"start": v(-56.15, 48.18) * mm, "mid": v(-58.99, 44.68) * mm, "end": v(-60, 40.3) * mm});
            skArc(sketch, "E80.2", {"start": v(56.15, 48.18) * mm, "mid": v(0, 67.5) * mm, "end": v(-56.15, 48.18) * mm});
            skArc(sketch, "E80.3", {"start": v(60, 40.3) * mm, "mid": v(58.99, 44.68) * mm, "end": v(56.15, 48.18) * mm});
            skLineSegment(sketch, "E80.4", {"start": v(60, 40.3) * mm, "end": v(60, -40.3) * mm});
            skArc(sketch, "E80.5", {"start": v(56.15, -48.18) * mm, "mid": v(58.99, -44.68) * mm, "end": v(60, -40.3) * mm});
            skArc(sketch, "E80.6", {"start": v(-56.15, -48.18) * mm, "mid": v(0, -67.5) * mm, "end": v(56.15, -48.18) * mm});
            skArc(sketch, "E80.7", {"start": v(-60, -40.3) * mm, "mid": v(-58.99, -44.68) * mm, "end": v(-56.15, -48.18) * mm});
            skCircle(sketch, "E80.8", {"center": v(-60, -67.5) * mm, "radius": 4 * mm});
            skCircle(sketch, "E80.9", {"center": v(-60, 67.5) * mm, "radius": 4 * mm});
            skCircle(sketch, "E80.10", {"center": v(60, 67.5) * mm, "radius": 4 * mm});
            skCircle(sketch, "E80.11", {"center": v(60, -67.5) * mm, "radius": 4 * mm});
            skArc(sketch, "E80.12", {"start": v(70, -90) * mm, "mid": v(77.07, -87.07) * mm, "end": v(80, -80) * mm});
            skLineSegment(sketch, "E80.13", {"start": v(-70, -90) * mm, "end": v(70, -90) * mm});
            skArc(sketch, "E80.14", {"start": v(-80, -80) * mm, "mid": v(-77.07, -87.07) * mm, "end": v(-70, -90) * mm});
            skLineSegment(sketch, "E80.15", {"start": v(-80, -80) * mm, "end": v(-80, 80) * mm});
            skArc(sketch, "E80.16", {"start": v(-70, 90) * mm, "mid": v(-77.07, 87.07) * mm, "end": v(-80, 80) * mm});
            skLineSegment(sketch, "E80.17", {"start": v(-70, 90) * mm, "end": v(70, 90) * mm});
            skArc(sketch, "E80.18", {"start": v(80, 80) * mm, "mid": v(77.07, 87.07) * mm, "end": v(70, 90) * mm});
            skLineSegment(sketch, "E80.19", {"start": v(80, -80) * mm, "end": v(80, 80) * mm});
            skLineSegment(sketch, "E80.20", {"start": v(80, -80) * mm, "end": v(80, 80) * mm});
            skLineSegment(sketch, "E81", {"start": v(0, 90) * mm, "end": v(0, 120) * mm, "construction": true});
            skPoint(sketch, "E81.endSnap0", {"position": v(0, 90) * mm});
            skLineSegment(sketch, "E82", {"start": v(-33, 90) * mm, "end": v(-15, 108) * mm});
            skLineSegment(sketch, "E83", {"start": v(-15, 108) * mm, "end": v(-15, 120) * mm});
            skArc(sketch, "E84", {"start": v(15, 120) * mm, "mid": v(0, 135) * mm, "end": v(-15, 120) * mm});
            skLineSegment(sketch, "E85", {"start": v(15, 120) * mm, "end": v(15, 108) * mm});
            skLineSegment(sketch, "E86", {"start": v(15, 108) * mm, "end": v(33, 90) * mm});
            skCircle(sketch, "E87", {"center": v(0, 120) * mm, "radius": 6 * mm});
            skLineSegment(sketch, "E88", {"start": v(-80, 0) * mm, "end": v(80, 0) * mm, "construction": true});
            skLineSegment(sketch, "E89.MirrorCS", {"start": v(15, -108) * mm, "end": v(33, -90) * mm});
            skLineSegment(sketch, "E90.MirrorCS", {"start": v(15, -120) * mm, "end": v(15, -108) * mm});
            skArc(sketch, "E91.MirrorCS", {"start": v(15, -120) * mm, "mid": v(0, -135) * mm, "end": v(-15, -120) * mm});
            skLineSegment(sketch, "E92.MirrorCS", {"start": v(-15, -108) * mm, "end": v(-15, -120) * mm});
            skLineSegment(sketch, "E93.MirrorCS", {"start": v(-33, -90) * mm, "end": v(-15, -108) * mm});
            skLineSegment(sketch, "E94.MirrorCS", {"start": v(0, -90) * mm, "end": v(0, -120) * mm, "construction": true});
            skCircle(sketch, "E95.MirrorC", {"center": v(0, -120) * mm, "radius": 6 * mm});
            skSolve(sketch);
        }
        {
            var Q0;
            Q0 = qSketchRegion(id + "F16", true);
            extrude(context, id + "F17", {"entities" : qUnion([Q0]), "depth" : 25 * mm});
        }
    });
